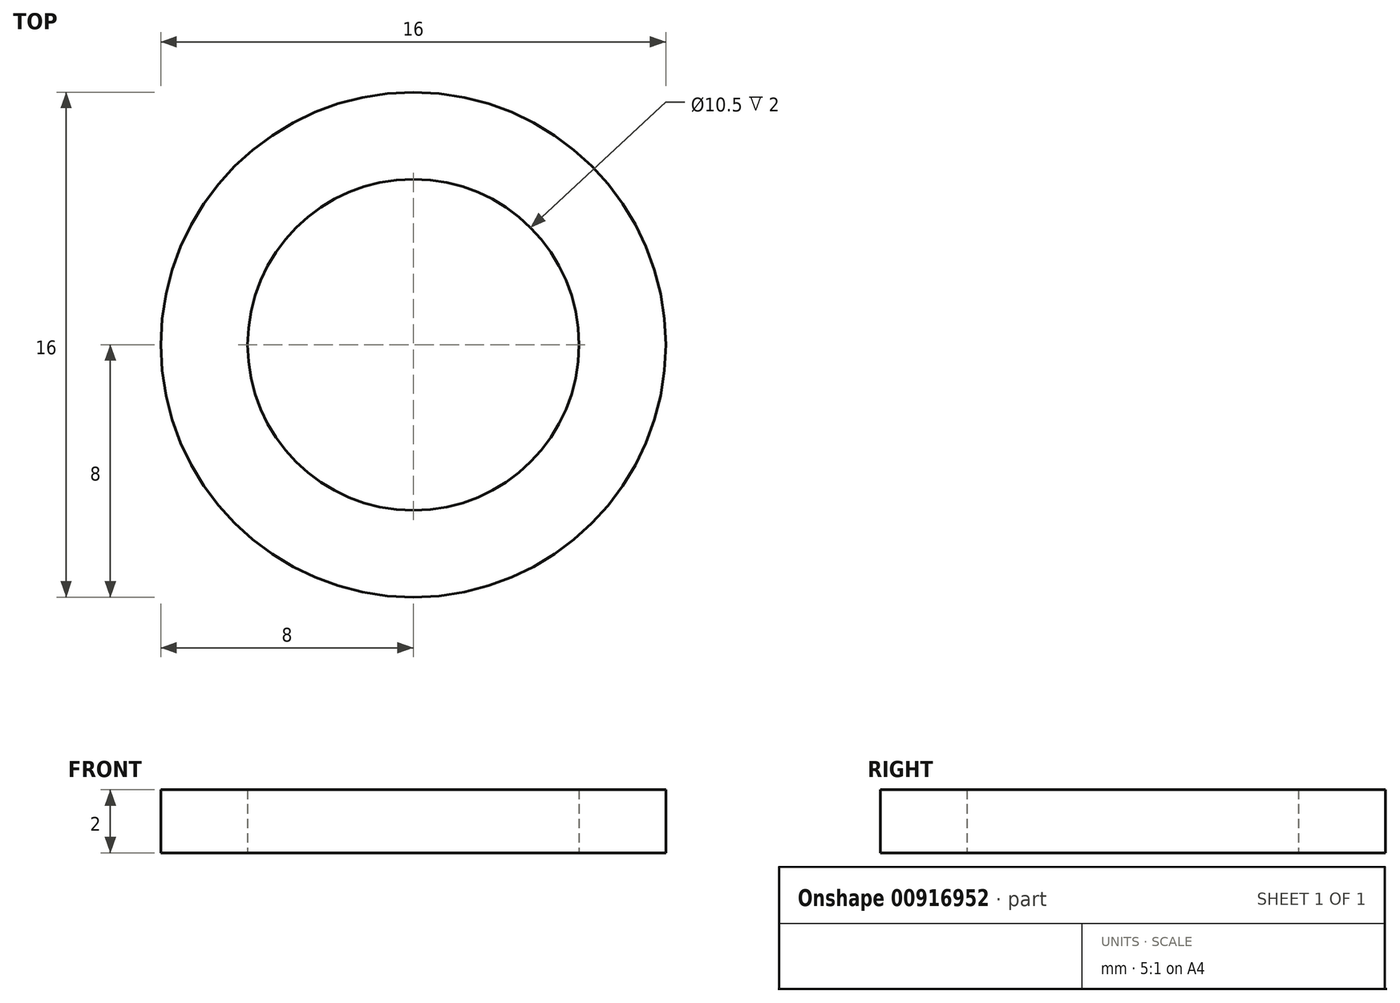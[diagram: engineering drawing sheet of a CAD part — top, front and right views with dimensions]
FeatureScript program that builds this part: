
annotation { "Feature Type Name" : "Feature", "Feature Type Description" : "" }
export const myFeature = defineFeature(function(context is Context, id is Id, definition is map)
    precondition{}
    {
        {
            var Q0;
            Q0=qCreatedBy(makeId("Top.planeOp"),FACE);
            var sketch = newSketch(context, id + "F0", { "sketchPlane" : qUnion([Q0])});
            skCircle(sketch, "E0", {"center": v(0, 0) * mm, "radius": 8 * mm});
            skCircle(sketch, "E1", {"center": v(0, 0) * mm, "radius": 5.25 * mm});
            skSolve(sketch);
        }
        {
            var Q0;
            Q0=makeQuery(id+"F0.imprint","IMPRINT",FACE,{"disambiguationData":[TD([[makeQuery(id+"F0.imprint","IMPRINT",EDGE,{"derivedFrom":sQuery(id+"F0.wireOp",EDGE,"E0")}),1.0]])]});
            extrude(context, id + "F1", {"entities" : qUnion([Q0]), "depth" : 2 * mm, "offsetDistance" : 25 * mm});
        }
    });
